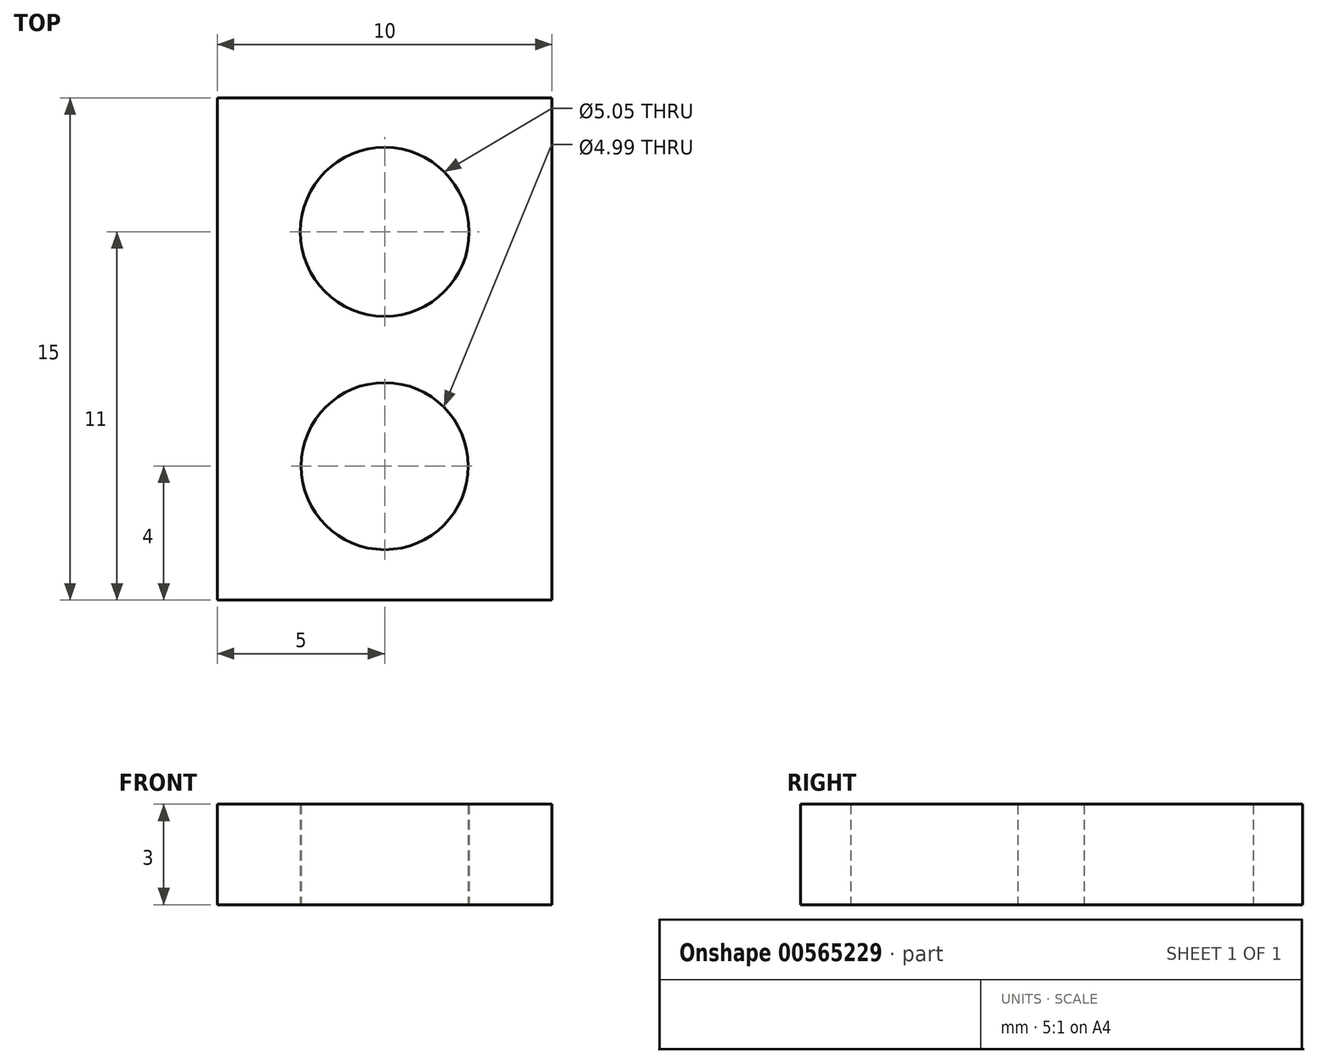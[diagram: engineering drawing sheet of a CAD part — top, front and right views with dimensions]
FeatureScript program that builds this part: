
annotation { "Feature Type Name" : "Feature", "Feature Type Description" : "" }
export const myFeature = defineFeature(function(context is Context, id is Id, definition is map)
    precondition{}
    {
        {
            var Q0;
            Q0=qCreatedBy(makeId("Top.planeOp"),FACE);
            var sketch = newSketch(context, id + "F0", { "sketchPlane" : qUnion([Q0])});
            skLineSegment(sketch, "E0.bottom", {"start": v(0, 0) * mm, "end": v(10, 0) * mm});
            skLineSegment(sketch, "E0.top", {"start": v(0, -15) * mm, "end": v(10, -15) * mm});
            skLineSegment(sketch, "E0.left", {"start": v(0, 0) * mm, "end": v(0, -15) * mm});
            skLineSegment(sketch, "E0.right", {"start": v(10, 0) * mm, "end": v(10, -15) * mm});
            skLineSegment(sketch, "E1", {"start": v(5, 0) * mm, "end": v(5, -15) * mm, "construction": true});
            skCircle(sketch, "E2", {"center": v(5, -4) * mm, "radius": 2.52 * mm});
            skCircle(sketch, "E3", {"center": v(5, -11) * mm, "radius": 2.5 * mm});
            skSolve(sketch);
        }
        {
            var Q0;
            Q0 = qSketchRegion(id + "F0", true);
            extrude(context, id + "F1", {"entities" : qUnion([Q0]), "depth" : 3 * mm, "offsetDistance" : 25 * mm});
        }
    });
